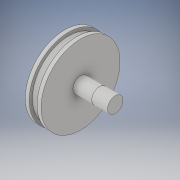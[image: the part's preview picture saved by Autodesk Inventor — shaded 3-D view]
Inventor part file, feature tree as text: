
AUTODESK INVENTOR PART (.ipt)
format: ipt  version: 2019 (Build 230136000, 136)  size: 124,416 bytes
history: native  units: in
note: dims shown in document units (in); Inventor stores cm internally (conversion verified against a paired STEP export)
features: revolve x1, sketch x1
ambient origin geometry x8: Origin, YZ Plane, XZ Plane, XY Plane, X Axis, Y Axis, Z Axis, Center Point
bodies: Solid1 (feature_tree)
feature tree (2):
  revolve  "Revolution1"  [1 undecoded]
  sketch  "Sketch1"  dims[d0=0.9843in d1=0.0984in d2=0.0787in d3=0.1969in d4=0.0984in d5=0.7953in d6=0.4724in d7=0.0039in d8=0.3937in d9=90.0deg]
note: 1 required parameter value undecoded (feature->parameter linkage not recoverable at this tier; creation-order binding heuristic only, values carry confidence <= 0.55)
